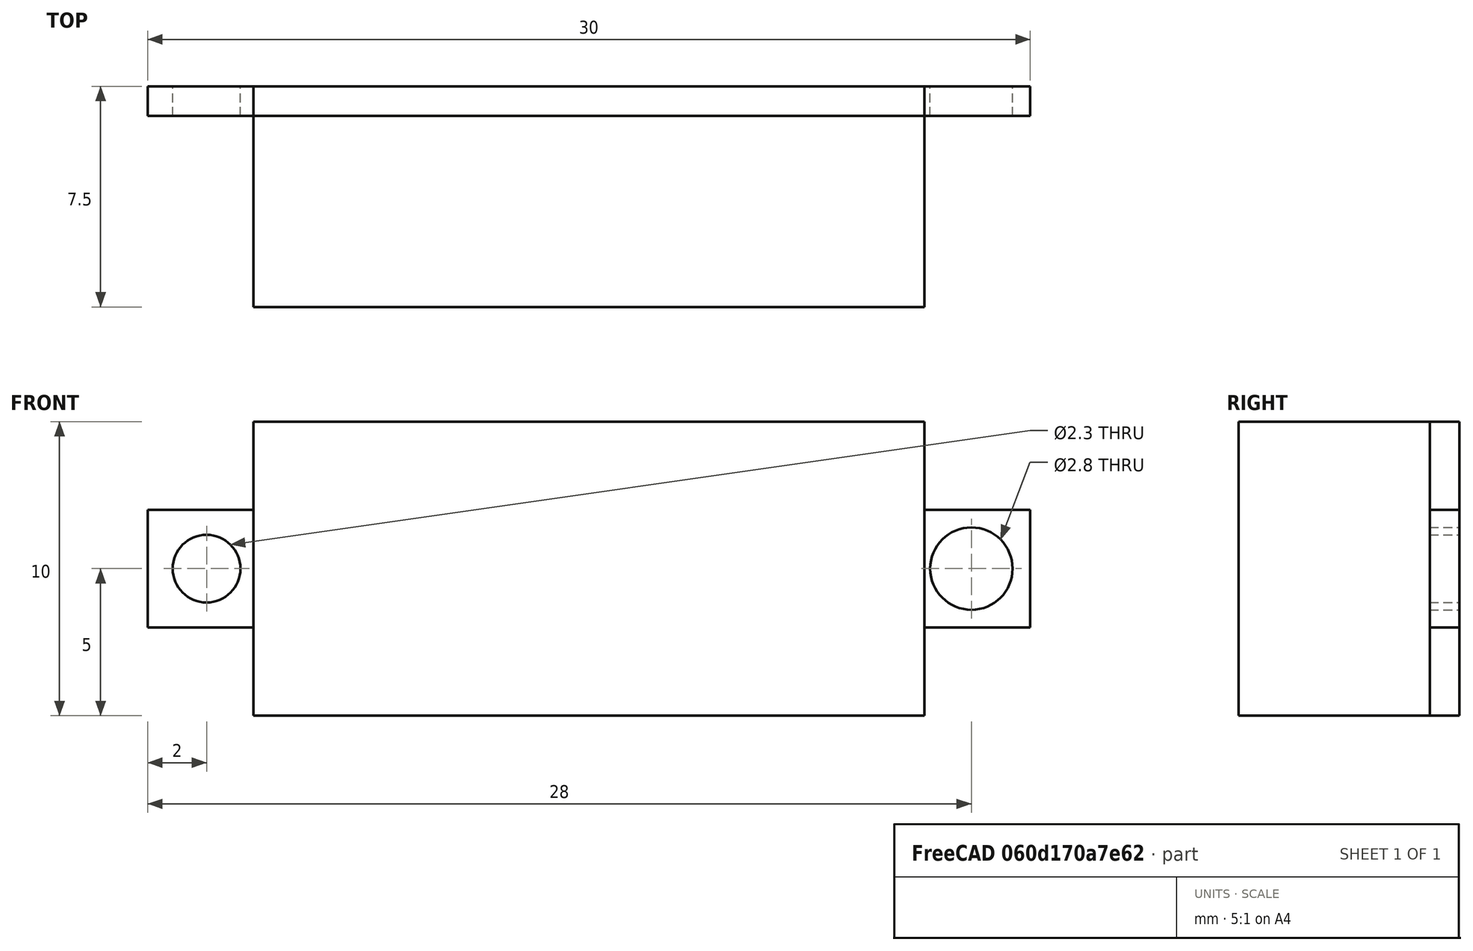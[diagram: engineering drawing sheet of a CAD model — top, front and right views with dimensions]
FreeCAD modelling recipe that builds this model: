
FCSTD DOCUMENT  (FreeCAD 0.19R24267 +148 (Git))
Label: voltm_003
License: All rights reserved
LicenseURL: http://en.wikipedia.org/wiki/All_rights_reserved
objects: Sketcher::SketchObject×1, PartDesign::Body×1, Part::Feature×1, Spreadsheet::Sheet×1, App::Part×1
note: 3 computed .brp shape members not serialized (recipe doc carries the construction recipe); baked Part::Feature solids carry a one-line shape summary decoded from their .brp

FEATURE [Sketcher::SketchObject] Sketch001
  FullyConstrained = true
  MapMode = 5
  Placement = pos=(0,0,0) rot=(1,0,0;1.5708rad)
  Support = -> [XZ_Plane001]
  sketch-geometry (7):
    g0: LineSegment StartX=-11.395 StartY=5.01 StartZ=0 EndX=11.395 EndY=5.01 EndZ=0
    g1: LineSegment StartX=11.395 StartY=5.01 StartZ=0 EndX=11.395 EndY=-5.01 EndZ=0
    g2: LineSegment StartX=11.395 StartY=-5.01 StartZ=0 EndX=-11.395 EndY=-5.01 EndZ=0
    g3: LineSegment StartX=-11.395 StartY=-5.01 StartZ=0 EndX=-11.395 EndY=5.01 EndZ=0
    g4: LineSegment StartX=-13.05 StartY=0 StartZ=0 EndX=13.05 EndY=0 EndZ=0
    g5: Circle CenterX=13.05 CenterY=0 CenterZ=0 NormalX=0 NormalY=0 NormalZ=1 AngleXU=0 Radius=1.15
    g6: Circle CenterX=-13.05 CenterY=0 CenterZ=0 NormalX=0 NormalY=0 NormalZ=1 AngleXU=0 Radius=1.15
  constraints (17):
    c: Coincident(g0,g1)
    c: Coincident(g1,g2)
    c: Coincident(g2,g3)
    c: Coincident(g3,g0)
    c: Horizontal(g2)
    c: Vertical(g1)
    c: PointOnObject(g4,g-1)
    c: DistanceY(g1,g1) = 10.02
    c: DistanceX(g4,g4) = 26.1
    c: DistanceX(g0,g0) = 22.79
    c: Coincident(g5,g4)
    c: Coincident(g6,g4)
    c: Equal(g6,g5)
    c: Diameter(g5) = 2.3
    c: Symmetric(g4,g4,g-2)
    c: Symmetric(g0,g2,g-1)
    c: Symmetric(g0,g0,g-2)
FEATURE [PartDesign::Body] Body  label="voltmBdy"
  Group = -> [Sketch001]
  Origin = -> Origin001
FEATURE [Part::Feature] Part__Feature003  label="LED DC Digital Voltmeter 5V Display grün"
  Placement = pos=(0,0,0) rot=(1,0,0;1.5708rad)
  shape: bbox 30 x 7.5 x 10 mm, 22 faces, 2 solids (baked)
FEATURE [Spreadsheet::Sheet] Spreadsheet  label="voltmSp"
  cells = A2=larg; B2(larg)=10; A3=long; B3(long)=22.8; A4=haut; B4(haut)=6.6; A5=trouDiam; B5(trouDiam)=2.3; A6=trouEntraxe; B6(trouEntraxe)=26
FEATURE [App::Part] Part  label="voltm"
  Group = -> [Body,Part__Feature003,Spreadsheet]
  Origin = -> Origin
